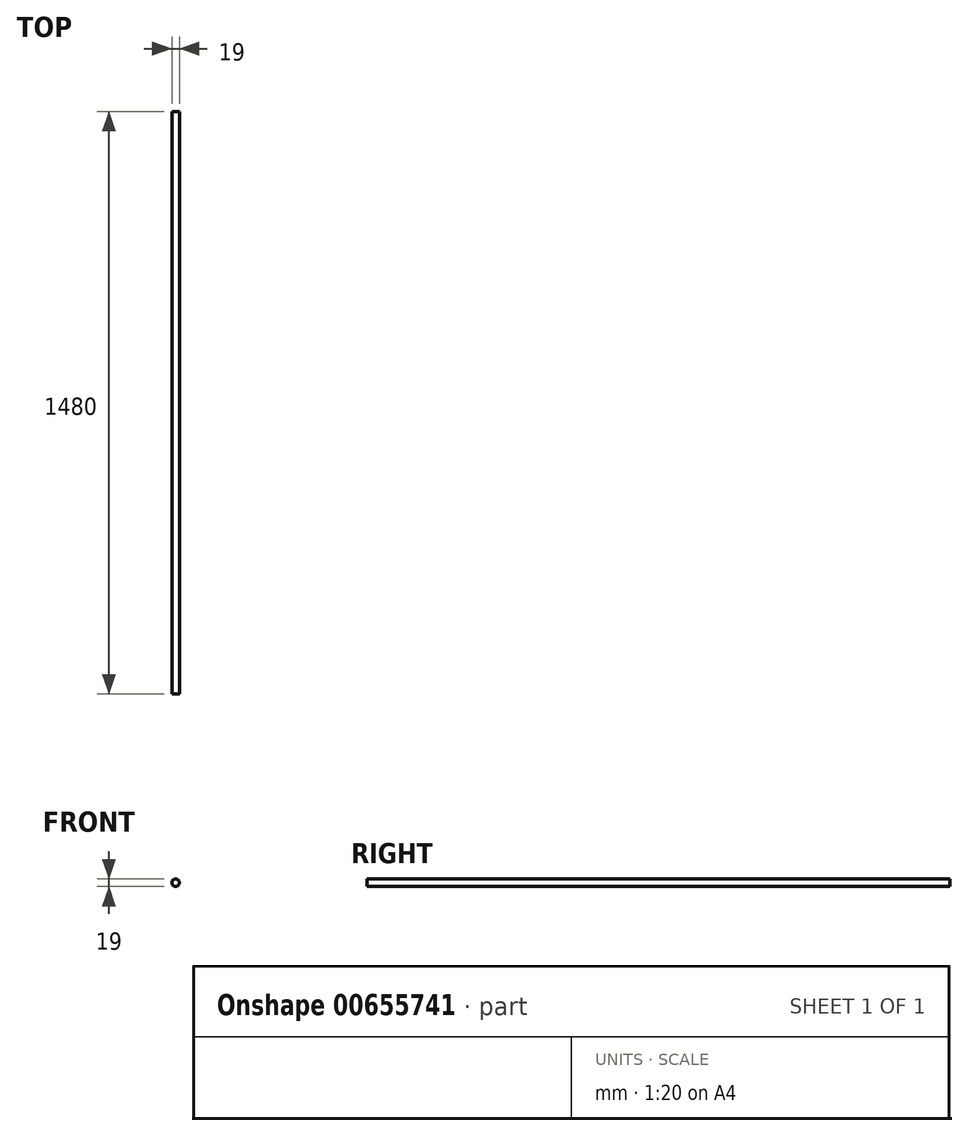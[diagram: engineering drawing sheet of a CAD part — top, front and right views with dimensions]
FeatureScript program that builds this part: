
annotation { "Feature Type Name" : "Feature", "Feature Type Description" : "" }
export const myFeature = defineFeature(function(context is Context, id is Id, definition is map)
    precondition{}
    {
        {
            var Q0;
            Q0=qCreatedBy(makeId("Front.planeOp"),FACE);
            var sketch = newSketch(context, id + "F0", { "sketchPlane" : qUnion([Q0])});
            skCircle(sketch, "E0", {"center": v(0, 0) * mm, "radius": 9.5 * mm});
            skSolve(sketch);
        }
        {
            var Q0;
            Q0=makeQuery(id+"F0.imprint","IMPRINT",FACE,{"disambiguationData":[TD([[makeQuery(id+"F0.imprint","IMPRINT",EDGE,{"derivedFrom":sQuery(id+"F0.wireOp",EDGE,"E0")}),1.0]])]});
            extrude(context, id + "F1", {"entities" : qUnion([Q0]), "depth" : 1480 * mm, "offsetDistance" : 25.4 * mm});
        }
    });
